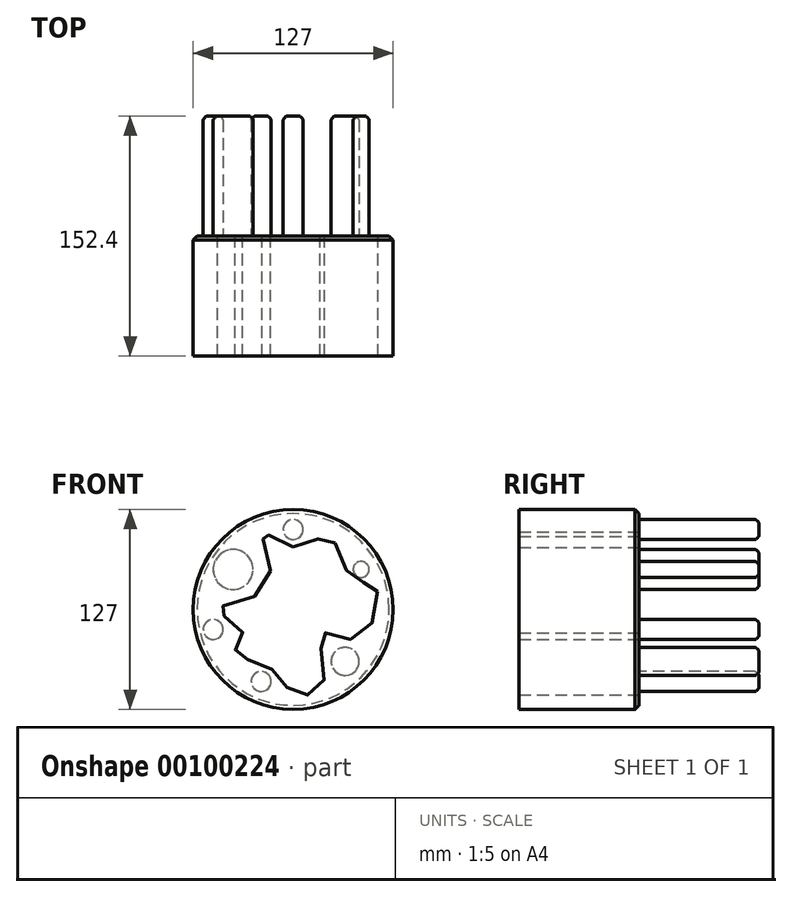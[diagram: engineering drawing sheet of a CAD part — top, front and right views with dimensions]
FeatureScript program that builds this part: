
annotation { "Feature Type Name" : "Feature", "Feature Type Description" : "" }
export const myFeature = defineFeature(function(context is Context, id is Id, definition is map)
    precondition{}
    {
        {
            var Q0;
            Q0=qCreatedBy(makeId("Front.planeOp"),FACE);
            var sketch = newSketch(context, id + "F0", { "sketchPlane" : qUnion([Q0])});
            skCircle(sketch, "E0", {"center": v(0, 0) * mm, "radius": 63.5 * mm});
            skFitSpline(sketch, "E1", {"points": [v(0, 39.57) * mm, v(23.06, 46.01) * mm, v(38.3, 18.85) * mm, v(52.17, 15.14) * mm, v(41.81, -18.27) * mm, v(17.98, -15.34) * mm, v(18.95, -47.38) * mm, v(0, -52.66) * mm, v(-16.22, -35.85) * mm, v(-36.93, -27.65) * mm, v(-32.24, -13.97) * mm, v(-48.06, 0) * mm, v(-16.41, 14.95) * mm, v(-19.73, 49.14) * mm, v(0, 39.57) * mm]});
            skSolve(sketch);
        }
        {
            var Q0;
            Q0=makeQuery(id+"F0.imprint","IMPRINT",FACE,{"disambiguationData":[TD([[makeQuery(id+"F0.imprint","IMPRINT",EDGE,{"derivedFrom":sQuery(id+"F0.wireOp",EDGE,"E0")}),1.0]])]});
            extrude(context, id + "F1", {"entities" : qUnion([Q0]), "depth" : 76.2 * mm});
        }
        {
            var Q0;
            Q0=qCreatedBy(makeId("Front.planeOp"),FACE);
            var sketch = newSketch(context, id + "F2", { "sketchPlane" : qUnion([Q0])});
            skCircle(sketch, "E2", {"center": v(-38.1, 25.4) * mm, "radius": 12.7 * mm});
            skCircle(sketch, "E3", {"center": v(33.02, -33.02) * mm, "radius": 8.9 * mm});
            skCircle(sketch, "E4", {"center": v(-50.8, -12.7) * mm, "radius": 6.35 * mm});
            skCircle(sketch, "E5", {"center": v(-20.32, -45.72) * mm, "radius": 6.35 * mm});
            skCircle(sketch, "E6", {"center": v(0, 50.8) * mm, "radius": 6.35 * mm});
            skCircle(sketch, "E7", {"center": v(43.18, 25.4) * mm, "radius": 5.08 * mm});
            skSolve(sketch);
        }
        {
            var Q0;
            Q0 = qSketchRegion(id + "F2", true);
            extrude(context, id + "F3", {"entities" : qUnion([Q0]), "operationType" : NewBodyOperationType.ADD, "oppositeDirection" : true, "depth" : 76.2 * mm});
        }
        {
            var Q0;
            Q0=makeQuery(id+"F3.opExtrude","CAP_EDGE",EDGE,{"disambiguationData":[OSD([sQuery(id+"F2.wireOp",EDGE,"E2")])],"isStart":false});
            var Q1;
            Q1=makeQuery(id+"F3.opExtrude","CAP_EDGE",EDGE,{"disambiguationData":[OSD([sQuery(id+"F2.wireOp",EDGE,"E6")])],"isStart":false});
            var Q2;
            Q2=makeQuery(id+"F3.opExtrude","CAP_EDGE",EDGE,{"disambiguationData":[OSD([sQuery(id+"F2.wireOp",EDGE,"E7")])],"isStart":false});
            var Q3;
            Q3=makeQuery(id+"F3.opExtrude","CAP_EDGE",EDGE,{"disambiguationData":[OSD([sQuery(id+"F2.wireOp",EDGE,"E3")])],"isStart":false});
            var Q4;
            Q4=makeQuery(id+"F3.opExtrude","CAP_EDGE",EDGE,{"disambiguationData":[OSD([sQuery(id+"F2.wireOp",EDGE,"E4")])],"isStart":false});
            var Q5;
            Q5=makeQuery(id+"F3.opExtrude","CAP_EDGE",EDGE,{"disambiguationData":[OSD([sQuery(id+"F2.wireOp",EDGE,"E5")])],"isStart":false});
            fillet(context, id + "F4", {"entities" : qUnion([Q0, Q1, Q2, Q3, Q4, Q5]), "radius" : 2.54 * mm, "tangentPropagation" : true, "rho" : .2, "crossSection" : FilletCrossSection.CONIC, "allowEdgeOverflow" : false});
        }
        {
            var Q0;
            Q0=makeQuery(id+"F1.opExtrude","CAP_EDGE",EDGE,{"disambiguationData":[OSD([sQuery(id+"F0.wireOp",EDGE,"E0")])],"isStart":true});
            chamfer(context, id + "F5", {"entities" : qUnion([Q0]), "width" : 2.54 * mm, "tangentPropagation" : true});
        }
    });
